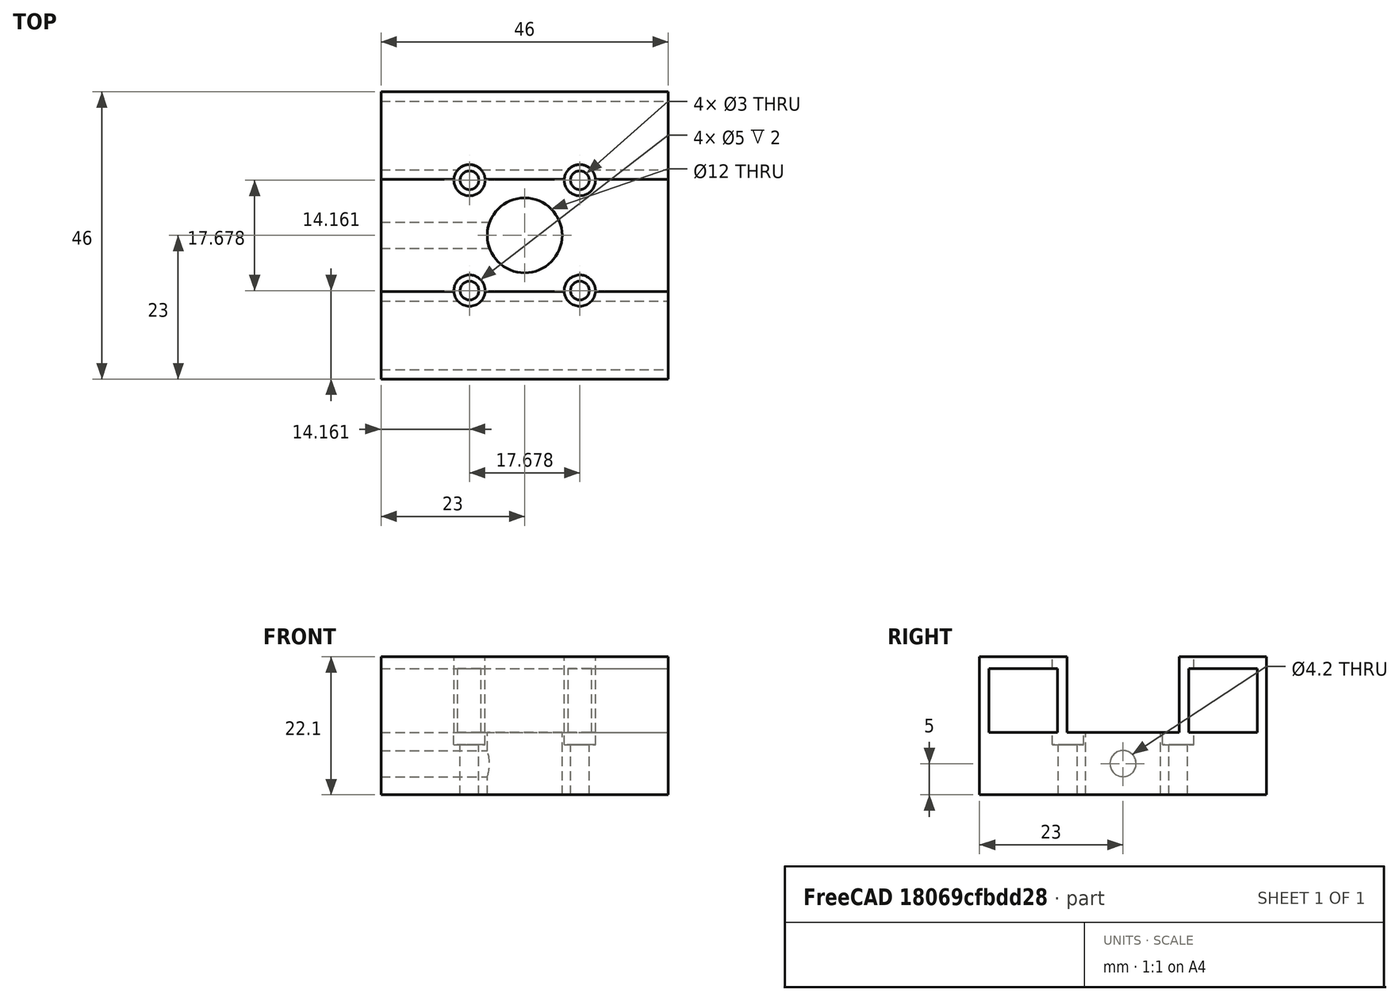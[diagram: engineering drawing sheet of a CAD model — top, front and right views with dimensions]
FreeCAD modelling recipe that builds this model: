
FCSTD DOCUMENT  (FreeCAD 0.18R16146 (Git))
Label: motor_mount
License: All rights reserved
LicenseURL: http://en.wikipedia.org/wiki/All_rights_reserved
objects: Part::Cylinder×14, Part::Box×5, Part::MultiFuse×5, Part::Cut×5
note: 29 computed .brp shape members not serialized (recipe doc carries the construction recipe); baked Part::Feature solids carry a one-line shape summary decoded from their .brp

FEATURE [Part::Box] Box022  label="Würfel022"
  AttacherType = Attacher::AttachEngine3D
  Height = 12.1
  Length = 46
  Placement = pos=(-23,-23,68) rot=(0,0,1;0rad)
  Width = 14
FEATURE [Part::Cylinder] Cylinder090  label="Zylinder087"
  Angle = 360
  AttacherType = Attacher::AttachEngine3D
  Height = 14
  Placement = pos=(-12.5,0,68) rot=(0,0,1;0rad)
  Radius = 2.5
FEATURE [Part::Cylinder] Cylinder079  label="Zylinder077"
  Angle = 360
  AttacherType = Attacher::AttachEngine3D
  Height = 10
  Placement = pos=(-12.5,0,58) rot=(0,0,1;0rad)
  Radius = 1.5
FEATURE [Part::Box] Box020  label="Würfel020"
  AttacherType = Attacher::AttachEngine3D
  Height = 12.1
  Length = 46
  Placement = pos=(-23,9,68) rot=(0,0,1;0rad)
  Width = 14
FEATURE [Part::Cylinder] Cylinder085  label="Zylinder083"
  Angle = 360
  AttacherType = Attacher::AttachEngine3D
  Height = 2
  Placement = pos=(0,12.5,66) rot=(0,0,1;0rad)
  Radius = 2.5
FEATURE [Part::Cylinder] Cylinder086  label="Zylinder084"
  Angle = 360
  AttacherType = Attacher::AttachEngine3D
  Height = 2
  Placement = pos=(0,-12.5,66) rot=(0,0,1;0rad)
  Radius = 2.5
FEATURE [Part::Box] Box024  label="Würfel024"
  AttacherType = Attacher::AttachEngine3D
  Height = 10.2
  Length = 46
  Placement = pos=(-23,10.5,68) rot=(0,0,1;0rad)
  Width = 11
FEATURE [Part::Box] Box025  label="Würfel025"
  AttacherType = Attacher::AttachEngine3D
  Height = 10.2
  Length = 46
  Placement = pos=(-23,-21.5,68) rot=(0,0,1;0rad)
  Width = 11
FEATURE [Part::Cylinder] Cylinder089  label="Zylinder086"
  Angle = 360
  AttacherType = Attacher::AttachEngine3D
  Height = 14
  Placement = pos=(12.5,0,68) rot=(0,0,1;0rad)
  Radius = 2.5
FEATURE [Part::Cylinder] Cylinder091  label="Zylinder088"
  Angle = 360
  AttacherType = Attacher::AttachEngine3D
  Height = 14
  Placement = pos=(0,12.5,68) rot=(0,0,1;0rad)
  Radius = 2.5
FEATURE [Part::Cylinder] Cylinder092  label="Zylinder089"
  Angle = 360
  AttacherType = Attacher::AttachEngine3D
  Height = 14
  Placement = pos=(0,-12.5,68) rot=(0,0,1;0rad)
  Radius = 2.5
FEATURE [Part::MultiFuse] Fusion025
  Shapes = -> [Box024,Box025]
FEATURE [Part::Cylinder] Cylinder087  label="axis002"
  Angle = 360
  AttacherType = Attacher::AttachEngine3D
  Height = 10
  Placement = pos=(0,0,58) rot=(0,0,1;0rad)
  Radius = 6
FEATURE [Part::Cylinder] Cylinder080  label="Zylinder078"
  Angle = 360
  AttacherType = Attacher::AttachEngine3D
  Height = 10
  Placement = pos=(12.5,0,58) rot=(0,0,1;0rad)
  Radius = 1.5
FEATURE [Part::MultiFuse] Fusion026
  Shapes = -> [Box022,Box020]
FEATURE [Part::Cut] Cut044
  Base = -> Fusion026
  Tool = -> Fusion025
FEATURE [Part::Cylinder] Cylinder088  label="Zylinder085"
  Angle = 360
  AttacherType = Attacher::AttachEngine3D
  Height = 24
  Placement = pos=(-23,0,63) rot=(0,1,0;1.5708rad)
  Radius = 2.1
FEATURE [Part::Box] Box019  label="Würfel019"
  AttacherType = Attacher::AttachEngine3D
  Height = 10
  Length = 46
  Placement = pos=(-23,-23,58) rot=(0,0,1;0rad)
  Width = 46
FEATURE [Part::Cylinder] Cylinder081  label="Zylinder079"
  Angle = 360
  AttacherType = Attacher::AttachEngine3D
  Height = 10
  Placement = pos=(0,12.5,58) rot=(0,0,1;0rad)
  Radius = 1.5
FEATURE [Part::Cylinder] Cylinder082  label="Zylinder080"
  Angle = 360
  AttacherType = Attacher::AttachEngine3D
  Height = 10
  Placement = pos=(0,-12.5,58) rot=(0,0,1;0rad)
  Radius = 1.5
FEATURE [Part::MultiFuse] Fusion027
  Placement = pos=(0,0,0) rot=(0,0,1;0.785398rad)
  Shapes = -> [Cylinder089,Cylinder091,Cylinder092,Cylinder090]
FEATURE [Part::Cut] Cut045
  Base = -> Cut044
  Tool = -> Fusion027
FEATURE [Part::Cylinder] Cylinder083  label="Zylinder081"
  Angle = 360
  AttacherType = Attacher::AttachEngine3D
  Height = 2
  Placement = pos=(12.5,0,66) rot=(0,0,1;0rad)
  Radius = 2.5
FEATURE [Part::Cylinder] Cylinder084  label="Zylinder082"
  Angle = 360
  AttacherType = Attacher::AttachEngine3D
  Height = 2
  Placement = pos=(-12.5,0,66) rot=(0,0,1;0rad)
  Radius = 2.5
FEATURE [Part::MultiFuse] Fusion023
  Placement = pos=(0,0,0) rot=(0,0,1;0.785398rad)
  Shapes = -> [Cylinder080,Cylinder083,Cylinder079,Cylinder084,Cylinder085,Cylinder086,Cylinder081,Cylinder082]
FEATURE [Part::Cut] Cut042
  Base = -> Box019
  Tool = -> Fusion023
FEATURE [Part::Cut] Cut043
  Base = -> Cut042
  Tool = -> Cylinder087
FEATURE [Part::MultiFuse] Fusion028
  Shapes = -> [Cut043,Cut045]
FEATURE [Part::Cut] Cut046  label="Motor_Mount"
  Base = -> Fusion028
  Tool = -> Cylinder088
